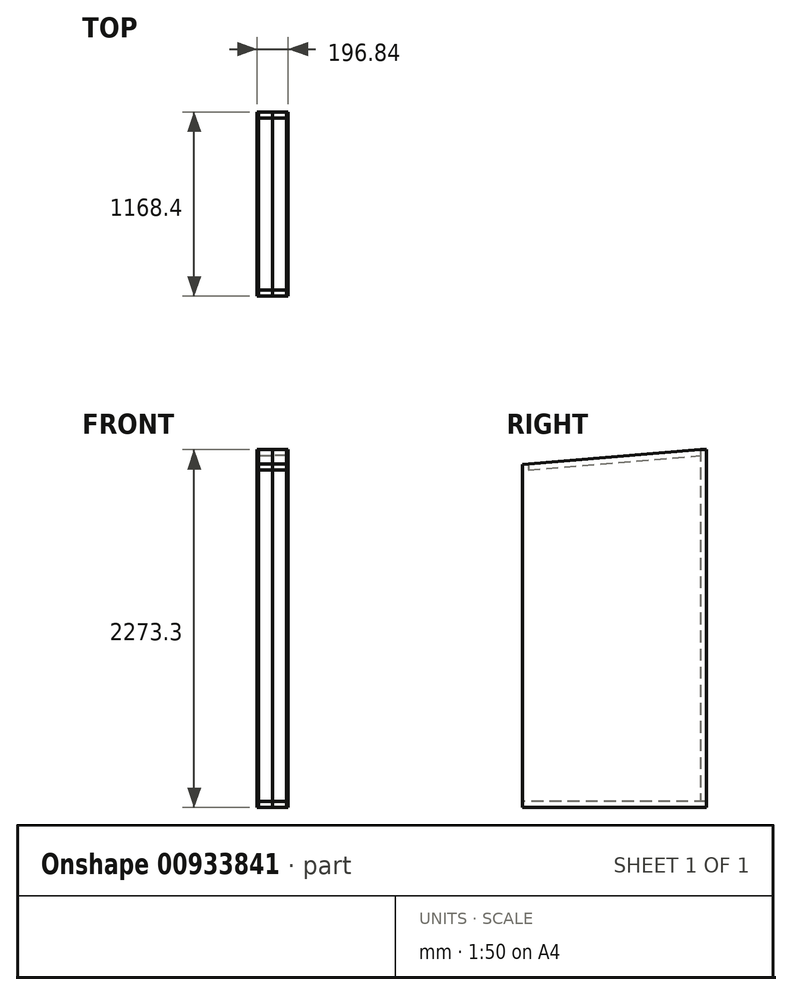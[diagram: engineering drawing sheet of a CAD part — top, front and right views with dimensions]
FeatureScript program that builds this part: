
annotation { "Feature Type Name" : "Feature", "Feature Type Description" : "" }
export const myFeature = defineFeature(function(context is Context, id is Id, definition is map)
    precondition{}
    {
        {
            var Q0;
            Q0=qCreatedBy(makeId("Right.planeOp"),FACE);
            var sketch = newSketch(context, id + "F0", { "sketchPlane" : qUnion([Q0])});
            skLineSegment(sketch, "E0.rect.bottom", {"start": v(-584.2, 1136.65) * mm, "end": v(584.2, 1136.65) * mm, "construction": true});
            skLineSegment(sketch, "E0.rect.top", {"start": v(-584.2, -1136.65) * mm, "end": v(584.2, -1136.65) * mm, "construction": true});
            skLineSegment(sketch, "E0.rect.left", {"start": v(-584.2, 1136.65) * mm, "end": v(-584.2, -1136.65) * mm, "construction": true});
            skLineSegment(sketch, "E0.rect.right", {"start": v(584.2, 1136.65) * mm, "end": v(584.2, -1136.65) * mm, "construction": true});
            skPoint(sketch, "E0.rect.middle", {"position": v(0, 0) * mm});
            skLineSegment(sketch, "E1.bottom", {"start": v(584.2, -1136.65) * mm, "end": v(-584.2, -1136.65) * mm});
            skLineSegment(sketch, "E1.top", {"start": v(584.2, -1098.55) * mm, "end": v(-584.2, -1098.55) * mm});
            skLineSegment(sketch, "E1.left", {"start": v(584.2, -1136.65) * mm, "end": v(584.2, -1098.55) * mm});
            skLineSegment(sketch, "E1.right", {"start": v(-584.2, -1136.65) * mm, "end": v(-584.2, -1098.55) * mm});
            skLineSegment(sketch, "E2.bottom", {"start": v(584.2, 1136.65) * mm, "end": v(546.1, 1136.65) * mm});
            skLineSegment(sketch, "E2.top", {"start": v(584.2, -1098.55) * mm, "end": v(546.1, -1098.55) * mm});
            skLineSegment(sketch, "E2.left", {"start": v(584.2, 1136.65) * mm, "end": v(584.2, -1098.55) * mm});
            skLineSegment(sketch, "E2.right", {"start": v(546.1, 1136.65) * mm, "end": v(546.1, -1098.55) * mm});
            skLineSegment(sketch, "E3.top", {"start": v(-584.2, -1098.55) * mm, "end": v(-546.1, -1098.55) * mm});
            skLineSegment(sketch, "E3.left", {"start": v(-584.2, 1043.43) * mm, "end": v(-584.2, -1098.55) * mm});
            skLineSegment(sketch, "E3.right", {"start": v(-546.1, 1046.57) * mm, "end": v(-546.1, -1098.55) * mm});
            skLineSegment(sketch, "E4", {"start": v(546.1, 1136.65) * mm, "end": v(-546.1, 1046.57) * mm});
            skLineSegment(sketch, "E5", {"start": v(-546.1, 1008.34) * mm, "end": v(546.1, 1098.42) * mm});
            skLineSegment(sketch, "E6", {"start": v(-546.1, 1046.57) * mm, "end": v(-584.2, 1043.43) * mm});
            skLineSegment(sketch, "E7", {"start": v(-473.4, 1052.57) * mm, "end": v(-685.8, 1035.05) * mm, "construction": true});
            skLineSegment(sketch, "E8", {"start": v(-685.8, 1035.05) * mm, "end": v(-685.8, -956.68) * mm, "construction": true});
            skLineSegment(sketch, "E9.bottom", {"start": v(139.7, -1098.55) * mm, "end": v(177.8, -1098.55) * mm});
            skLineSegment(sketch, "E9.top", {"start": v(139.7, 1068.05) * mm, "end": v(177.8, 1068.05) * mm});
            skLineSegment(sketch, "E9.left", {"start": v(139.7, -1098.55) * mm, "end": v(139.7, 1068.05) * mm});
            skLineSegment(sketch, "E9.right", {"start": v(177.8, -1098.55) * mm, "end": v(177.8, 1068.05) * mm});
            skLineSegment(sketch, "E10.bottom", {"start": v(-266.7, -1098.55) * mm, "end": v(-228.6, -1098.55) * mm});
            skLineSegment(sketch, "E10.top", {"start": v(-266.7, 1034.53) * mm, "end": v(-228.6, 1034.53) * mm});
            skLineSegment(sketch, "E10.left", {"start": v(-266.7, -1098.55) * mm, "end": v(-266.7, 1034.53) * mm});
            skLineSegment(sketch, "E10.right", {"start": v(-228.6, -1098.55) * mm, "end": v(-228.6, 1034.53) * mm});
            skLineSegment(sketch, "E11", {"start": v(139.7, 1064.9) * mm, "end": v(177.8, 1068.05) * mm});
            skLineSegment(sketch, "E12", {"start": v(-228.6, 1034.53) * mm, "end": v(-266.7, 1031.39) * mm});
            skLineSegment(sketch, "E13", {"start": v(-266.7, 1031.39) * mm, "end": v(-228.6, 1034.53) * mm});
            skSolve(sketch);
        }
        {
            var Q0;
            {var subQ3=sQuery(id+"F0.wireOp",EDGE,"E3.top");Q0=makeQuery(id+"F0.imprint","IMPRINT",FACE,{"disambiguationData":[TD([[makeQuery(id+"F0.imprint","IMPRINT",EDGE,{"derivedFrom":subQ3}),1.0]])]});}
            var Q1;
            {var subQ3=sQuery(id+"F0.wireOp",EDGE,"E2.bottom");Q1=makeQuery(id+"F0.imprint","IMPRINT",FACE,{"disambiguationData":[TD([[makeQuery(id+"F0.imprint","IMPRINT",EDGE,{"derivedFrom":subQ3}),1.0]])]});}
            var Q2;
            {var subQ0=sQuery(id+"F0.wireOp",EDGE,"E9.bottom");Q2=makeQuery(id+"F0.imprint","IMPRINT",FACE,{"disambiguationData":[TD([[makeQuery(id+"F0.imprint","IMPRINT",EDGE,{"derivedFrom":subQ0}),1.0]])]});}
            var Q3;
            {var subQ0=sQuery(id+"F0.wireOp",EDGE,"E10.bottom");Q3=makeQuery(id+"F0.imprint","IMPRINT",FACE,{"disambiguationData":[TD([[makeQuery(id+"F0.imprint","IMPRINT",EDGE,{"derivedFrom":subQ0}),1.0]])]});}
            extrude(context, id + "F1", {"entities" : qUnion([Q0, Q1, Q2, Q3]), "depth" : 88.9 * mm, "offsetDistance" : 25.4 * mm});
        }
        {
            var Q0;
            {var subQ1=sQuery(id+"F0.wireOp",EDGE,"E4");Q0=makeQuery(id+"F0.imprint","IMPRINT",FACE,{"disambiguationData":[TD([[makeQuery(id+"F0.imprint","IMPRINT",EDGE,{"derivedFrom":subQ1}),1.0]])]});}
            var Q1;
            Q1=makeQuery(id+"F0.imprint","IMPRINT",FACE,{"disambiguationData":[TD([[makeQuery(id+"F0.imprint","IMPRINT",EDGE,{"derivedFrom":sQuery(id+"F0.wireOp",EDGE,"E1.bottom")}),-1.0]])]});
            var Q2;
            {var subQ0=sQuery(id+"F0.wireOp",EDGE,"E9.top");Q2=makeQuery(id+"F0.imprint","IMPRINT",FACE,{"disambiguationData":[TD([[makeQuery(id+"F0.imprint","IMPRINT",EDGE,{"derivedFrom":subQ0}),-1.0]])]});}
            var Q3;
            {var subQ0=sQuery(id+"F0.wireOp",EDGE,"E10.top");Q3=makeQuery(id+"F0.imprint","IMPRINT",FACE,{"disambiguationData":[TD([[makeQuery(id+"F0.imprint","IMPRINT",EDGE,{"derivedFrom":subQ0}),-1.0]])]});}
            extrude(context, id + "F2", {"entities" : qUnion([Q0, Q1, Q2, Q3]), "depth" : 88.9 * mm, "offsetDistance" : 25.4 * mm});
        }
        {
            var Q0;
            Q0=makeQuery(id+"F1.opExtrude","CAP_FACE",FACE,{"disambiguationData":[OSD([sQuery(id+"F0.wireOp",EDGE,"E2.bottom"),sQuery(id+"F0.wireOp",EDGE,"E2.top"),sQuery(id+"F0.wireOp",EDGE,"E2.left"),sQuery(id+"F0.wireOp",EDGE,"E2.right")])],"isStart":false});
            var sketch = newSketch(context, id + "F3", { "sketchPlane" : qUnion([Q0])});
            skLineSegment(sketch, "E14", {"start": v(546.1, 1136.65) * mm, "end": v(-584.2, 1043.43) * mm});
            skLineSegment(sketch, "E15", {"start": v(-584.2, 1043.43) * mm, "end": v(-584.2, -1136.65) * mm});
            skLineSegment(sketch, "E16", {"start": v(-584.2, -1136.65) * mm, "end": v(584.2, -1136.65) * mm});
            skLineSegment(sketch, "E17", {"start": v(584.2, -1136.65) * mm, "end": v(584.2, 1136.65) * mm});
            skLineSegment(sketch, "E18", {"start": v(584.2, 1136.65) * mm, "end": v(546.1, 1136.65) * mm});
            skSolve(sketch);
        }
        {
            var Q0;
            Q0=qSketchRegion(id+"F3",true);
            extrude(context, id + "F4", {"entities" : qUnion([Q0]), "depth" : 9.52 * mm});
        }
        {
            var Q0;
            Q0=makeQuery(id+"F1.opExtrude","SWEPT_BODY",BODY,{"disambiguationData":[OSD([sQuery(id+"F0.wireOp",EDGE,"E2.bottom"),sQuery(id+"F0.wireOp",EDGE,"E2.top"),sQuery(id+"F0.wireOp",EDGE,"E2.left"),sQuery(id+"F0.wireOp",EDGE,"E2.right")])]});
            var Q1;
            Q1=makeQuery(id+"F1.opExtrude","SWEPT_BODY",BODY,{"disambiguationData":[OSD([sQuery(id+"F0.wireOp",EDGE,"E3.top"),sQuery(id+"F0.wireOp",EDGE,"E3.left"),sQuery(id+"F0.wireOp",EDGE,"E3.right"),sQuery(id+"F0.wireOp",EDGE,"E6")])]});
            var Q2;
            Q2=makeQuery(id+"F2.opExtrude","SWEPT_BODY",BODY,{"disambiguationData":[OSD([sQuery(id+"F0.wireOp",EDGE,"E1.bottom"),sQuery(id+"F0.wireOp",EDGE,"E1.top"),sQuery(id+"F0.wireOp",EDGE,"E1.left"),sQuery(id+"F0.wireOp",EDGE,"E1.right"),sQuery(id+"F0.wireOp",EDGE,"E2.top"),sQuery(id+"F0.wireOp",EDGE,"E3.top")])]});
            var Q3;
            Q3=makeQuery(id+"F2.opExtrude","SWEPT_BODY",BODY,{"disambiguationData":[OSD([sQuery(id+"F0.wireOp",EDGE,"E2.right"),sQuery(id+"F0.wireOp",EDGE,"E3.right"),sQuery(id+"F0.wireOp",EDGE,"E4"),sQuery(id+"F0.wireOp",EDGE,"E5")])]});
            var Q4;
            Q4=makeQuery(id+"F4.opExtrude","SWEPT_BODY",BODY,{"disambiguationData":[OSD([sQuery(id+"F3.wireOp",EDGE,"E14"),sQuery(id+"F3.wireOp",EDGE,"E15"),sQuery(id+"F3.wireOp",EDGE,"E16"),sQuery(id+"F3.wireOp",EDGE,"E17"),sQuery(id+"F3.wireOp",EDGE,"E18")])]});
            var Q5;
            Q5=qCreatedBy(makeId("Right.planeOp"),FACE);
            mirror(context, id + "F5", {"entities" : qUnion([Q0, Q1, Q2, Q3, Q4]), "mirrorPlane" : qUnion([Q5])});
        }
    });
